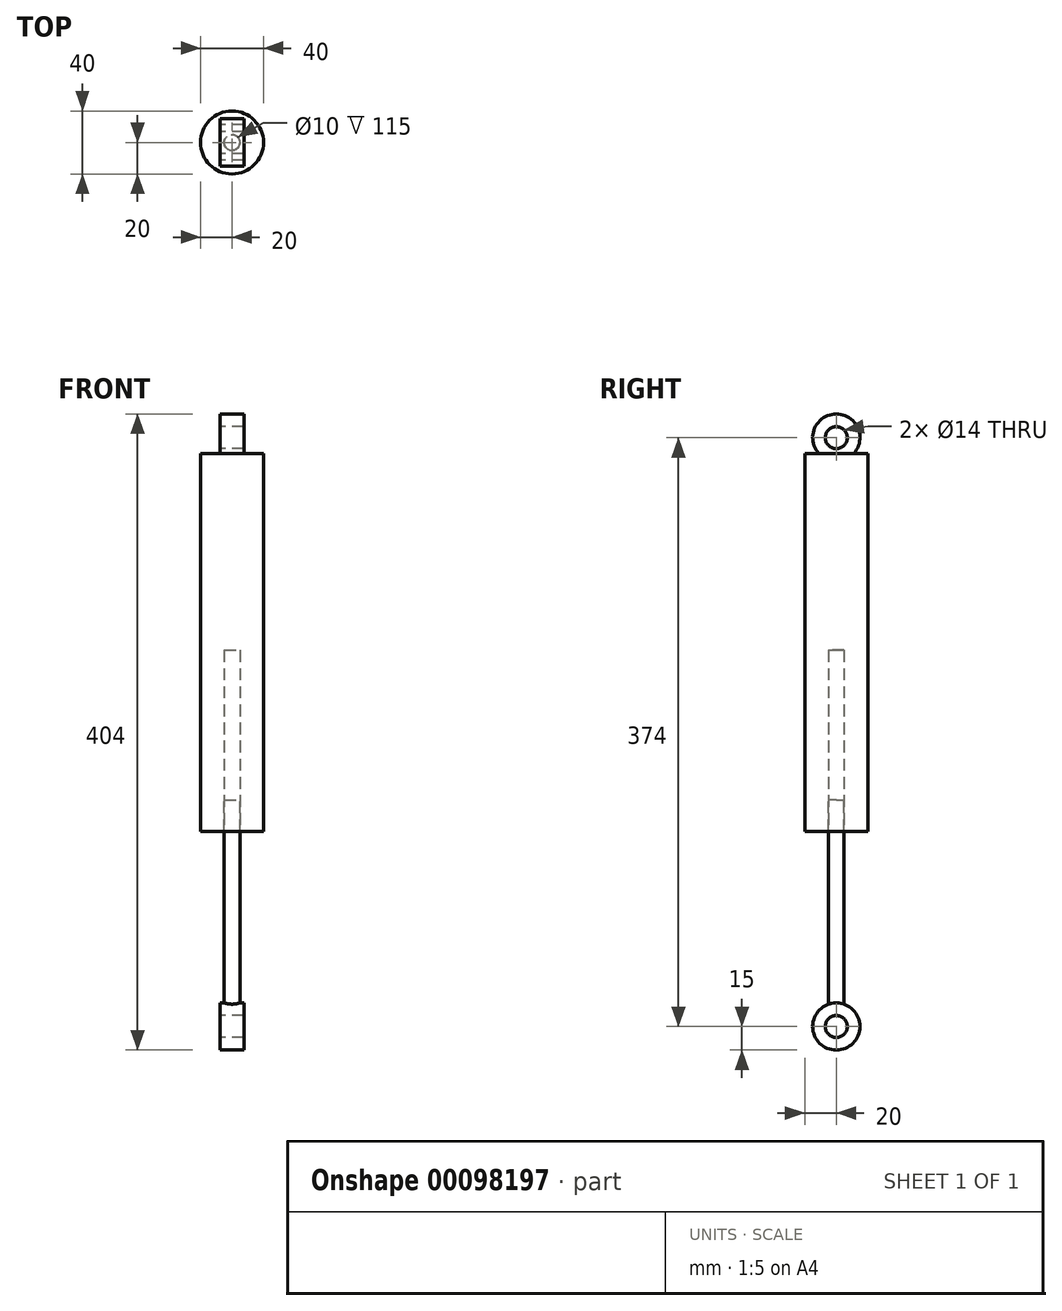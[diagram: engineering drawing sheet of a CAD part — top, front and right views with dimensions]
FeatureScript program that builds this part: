
annotation { "Feature Type Name" : "Feature", "Feature Type Description" : "" }
export const myFeature = defineFeature(function(context is Context, id is Id, definition is map)
    precondition{}
    {
        {
            var Q0;
            Q0=qCreatedBy(makeId("Top.planeOp"),FACE);
            var sketch = newSketch(context, id + "F0", { "sketchPlane" : qUnion([Q0])});
            skCircle(sketch, "E0", {"center": v(0, 0) * mm, "radius": 20 * mm});
            skSolve(sketch);
        }
        {
            var Q0;
            Q0=qSketchRegion(id+"F0",true);
            extrude(context, id + "F1", {"entities" : qUnion([Q0]), "depth" : 240 * mm});
        }
        {
            var Q0;
            Q0=qCreatedBy(makeId("Right.planeOp"),FACE);
            var sketch = newSketch(context, id + "F2", { "sketchPlane" : qUnion([Q0])});
            skCircle(sketch, "E1", {"center": v(0, 250) * mm, "radius": 7 * mm});
            skCircle(sketch, "E2", {"center": v(0, 250) * mm, "radius": 15 * mm});
            skSolve(sketch);
        }
        {
            var Q0;
            Q0=qSketchRegion(id+"F2",true);
            extrude(context, id + "F3", {"entities" : qUnion([Q0]), "operationType" : NewBodyOperationType.ADD, "endBound" : BoundingType.SYMMETRIC, "depth" : 15 * mm});
        }
        {
            var Q0;
            Q0=makeQuery(id+"F1.opExtrude","CAP_FACE",FACE,{"disambiguationData":[OSD([sQuery(id+"F0.wireOp",EDGE,"E0")])],"isStart":true});
            var sketch = newSketch(context, id + "F4", { "sketchPlane" : qUnion([Q0])});
            skCircle(sketch, "E3", {"center": v(0, 0) * mm, "radius": 5 * mm});
            skSolve(sketch);
        }
        {
            var Q0;
            Q0=qSketchRegion(id+"F4",true);
            extrude(context, id + "F5", {"entities" : qUnion([Q0]), "operationType" : NewBodyOperationType.REMOVE, "oppositeDirection" : true, "depth" : 115 * mm});
        }
        {
            var Q0;
            Q0=qSketchRegion(id+"F4",true);
            extrude(context, id + "F6", {"entities" : qUnion([Q0]), "depth" : 114 * mm, "hasSecondDirection" : true, "secondDirectionOppositeDirection" : true, "secondDirectionDepth" : 20 * mm});
        }
        {
            var Q0;
            Q0=qCreatedBy(makeId("Right.planeOp"),FACE);
            var sketch = newSketch(context, id + "F7", { "sketchPlane" : qUnion([Q0])});
            skCircle(sketch, "E4", {"center": v(0, -124) * mm, "radius": 7 * mm});
            skCircle(sketch, "E5", {"center": v(0, -124) * mm, "radius": 15 * mm});
            skSolve(sketch);
        }
        {
            var Q0;
            Q0=qSketchRegion(id+"F7",true);
            extrude(context, id + "F8", {"entities" : qUnion([Q0]), "operationType" : NewBodyOperationType.ADD, "endBound" : BoundingType.SYMMETRIC, "depth" : 15 * mm});
        }
    });
